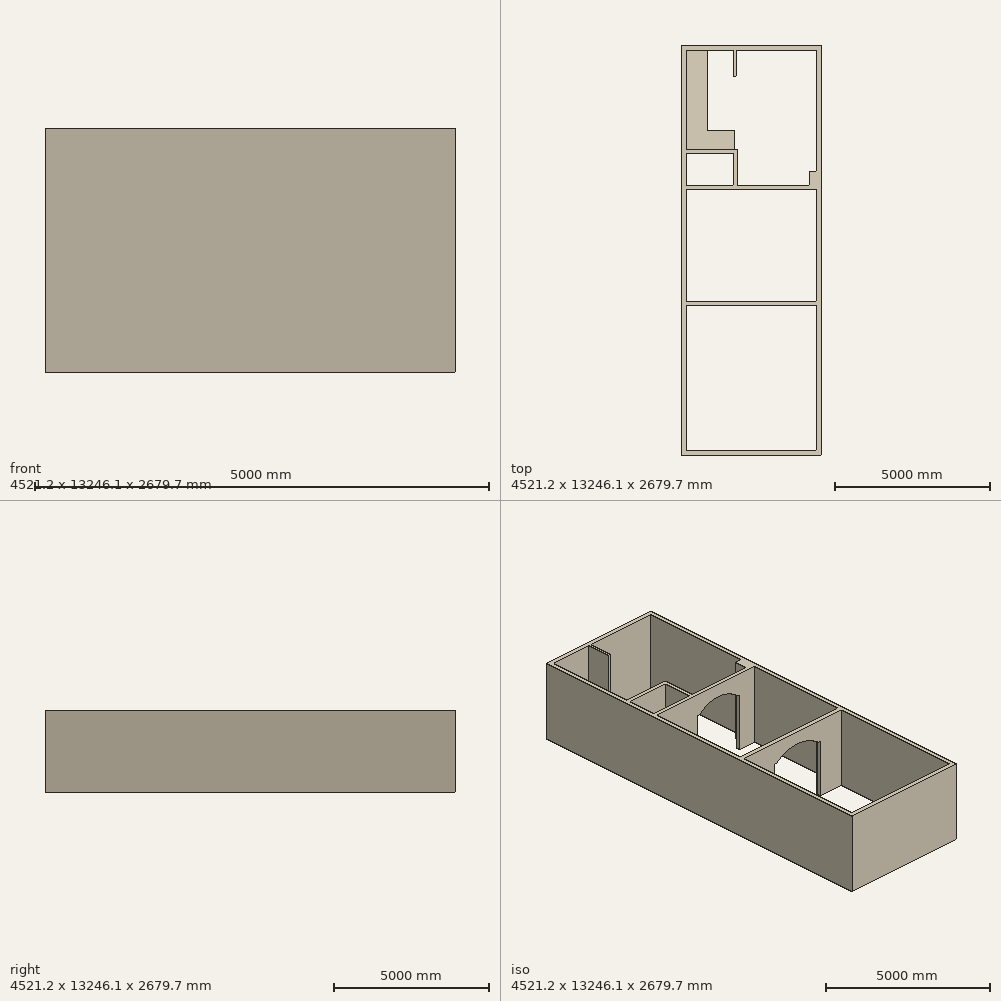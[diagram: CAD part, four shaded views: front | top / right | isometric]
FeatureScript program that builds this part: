
annotation { "Feature Type Name" : "Feature", "Feature Type Description" : "" }
export const myFeature = defineFeature(function(context is Context, id is Id, definition is map)
    precondition{}
    {
        {
            var Q0;
            Q0=qCreatedBy(makeId("Top.planeOp"),FACE);
            var sketch = newSketch(context, id + "F0", { "sketchPlane" : qUnion([Q0])});
            skLineSegment(sketch, "E0.bottom", {"start": v(0, 0) * mm, "end": v(4216.4, 0) * mm});
            skLineSegment(sketch, "E0.top", {"start": v(0, 12941.3) * mm, "end": v(1536.7, 12941.3) * mm});
            skLineSegment(sketch, "E0.left", {"start": v(0, 0) * mm, "end": v(0, 4686.3) * mm});
            skLineSegment(sketch, "E0.right", {"start": v(4216.4, 0) * mm, "end": v(4216.4, 4686.3) * mm});
            skLineSegment(sketch, "E1.bottom", {"start": v(4216.4, 4686.3) * mm, "end": v(3314.7, 4686.3) * mm});
            skLineSegment(sketch, "E1.top", {"start": v(4216.4, 4838.7) * mm, "end": v(3314.7, 4838.7) * mm});
            skLineSegment(sketch, "E1.right", {"start": v(3314.7, 4686.3) * mm, "end": v(3314.7, 4838.7) * mm});
            skLineSegment(sketch, "E2.0", {"start": v(-152.4, 13093.7) * mm, "end": v(4368.8, 13093.7) * mm});
            skLineSegment(sketch, "E2.1", {"start": v(-152.4, -152.4) * mm, "end": v(-152.4, 13093.7) * mm});
            skLineSegment(sketch, "E2.2", {"start": v(-152.4, -152.4) * mm, "end": v(4368.8, -152.4) * mm});
            skLineSegment(sketch, "E2.3", {"start": v(4368.8, -152.4) * mm, "end": v(4368.8, 13093.7) * mm});
            skLineSegment(sketch, "E3.trimOffspring", {"start": v(4216.4, 4838.7) * mm, "end": v(4216.4, 8445.5) * mm});
            skLineSegment(sketch, "E4", {"start": v(4216.4, 8445.5) * mm, "end": v(3581.4, 8445.5) * mm});
            skLineSegment(sketch, "E5", {"start": v(3581.4, 8445.5) * mm, "end": v(3581.4, 8572.5) * mm});
            skLineSegment(sketch, "E6", {"start": v(3581.4, 8572.5) * mm, "end": v(3987.8, 8572.5) * mm});
            skLineSegment(sketch, "E7.trimOffspring", {"start": v(4216.4, 9029.7) * mm, "end": v(4216.4, 12941.3) * mm});
            skLineSegment(sketch, "E8", {"start": v(3987.8, 8572.5) * mm, "end": v(3987.8, 9029.7) * mm});
            skLineSegment(sketch, "E9", {"start": v(3987.8, 9029.7) * mm, "end": v(4216.4, 9029.7) * mm});
            skLineSegment(sketch, "E10", {"start": v(1752.6, 8445.5) * mm, "end": v(0, 8445.5) * mm});
            skLineSegment(sketch, "E11", {"start": v(1752.6, 8445.5) * mm, "end": v(1752.6, 8572.5) * mm});
            skLineSegment(sketch, "E12", {"start": v(1752.6, 8572.5) * mm, "end": v(1663.7, 8572.5) * mm});
            skLineSegment(sketch, "E13", {"start": v(1663.7, 8572.5) * mm, "end": v(1663.7, 9740.9) * mm});
            skLineSegment(sketch, "E14", {"start": v(1663.7, 9740.9) * mm, "end": v(0, 9740.9) * mm});
            skLineSegment(sketch, "E15.0", {"start": v(1536.7, 9613.9) * mm, "end": v(0, 9613.9) * mm});
            skLineSegment(sketch, "E15.1", {"start": v(1536.7, 8572.5) * mm, "end": v(1536.7, 9613.9) * mm});
            skLineSegment(sketch, "E16", {"start": v(1536.7, 8572.5) * mm, "end": v(0, 8572.5) * mm});
            skLineSegment(sketch, "E17.trimOffspring", {"start": v(0, 8572.5) * mm, "end": v(0, 9613.9) * mm});
            skLineSegment(sketch, "E18.trimOffspring", {"start": v(0, 9740.9) * mm, "end": v(0, 12941.3) * mm});
            skLineSegment(sketch, "E19.top", {"start": v(1536.7, 12077.7) * mm, "end": v(1625.6, 12077.7) * mm});
            skLineSegment(sketch, "E19.left", {"start": v(1536.7, 12941.3) * mm, "end": v(1536.7, 12077.7) * mm});
            skLineSegment(sketch, "E19.right", {"start": v(1625.6, 12941.3) * mm, "end": v(1625.6, 12077.7) * mm});
            skLineSegment(sketch, "E20.trimOffspring", {"start": v(1625.6, 12941.3) * mm, "end": v(4216.4, 12941.3) * mm});
            skLineSegment(sketch, "E21.bottom", {"start": v(1333.5, 4838.7) * mm, "end": v(0, 4838.7) * mm});
            skLineSegment(sketch, "E21.top", {"start": v(1333.5, 4686.3) * mm, "end": v(0, 4686.3) * mm});
            skLineSegment(sketch, "E21.left", {"start": v(1333.5, 4838.7) * mm, "end": v(1333.5, 4686.3) * mm});
            skLineSegment(sketch, "E22.trimOffspring", {"start": v(0, 4838.7) * mm, "end": v(0, 8445.5) * mm});
            skSolve(sketch);
        }
        {
            var Q0;
            Q0=makeQuery(id+"F0.imprint","IMPRINT",FACE,{"disambiguationData":[TD([[makeQuery(id+"F0.imprint","IMPRINT",EDGE,{"derivedFrom":sQuery(id+"F0.wireOp",EDGE,"E0.bottom")}),-1.0]])]});
            extrude(context, id + "F1", {"entities" : qUnion([Q0]), "depth" : 2679.7 * mm});
        }
        {
            var Q0;
            Q0=makeQuery(id+"F1.opExtrude","SWEPT_FACE",FACE,{"disambiguationData":[OSD([sQuery(id+"F0.wireOp",EDGE,"E21.top")])]});
            var sketch = newSketch(context, id + "F2", { "sketchPlane" : qUnion([Q0])});
            skLineSegment(sketch, "E23.bottom", {"start": v(1333.5, 2679.7) * mm, "end": v(3314.7, 2679.7) * mm});
            skLineSegment(sketch, "E23.top", {"start": v(1333.5, 1930.4) * mm, "end": v(1422.4, 1930.4) * mm});
            skLineSegment(sketch, "E23.left", {"start": v(1333.5, 2679.7) * mm, "end": v(1333.5, 1930.4) * mm});
            skLineSegment(sketch, "E23.right", {"start": v(3314.7, 2679.7) * mm, "end": v(3314.7, 1930.4) * mm});
            skLineSegment(sketch, "E24", {"start": v(2324.1, 1930.4) * mm, "end": v(2324.1, 2679.7) * mm, "construction": true});
            skLineSegment(sketch, "E25", {"start": v(1422.4, 1930.4) * mm, "end": v(1422.4, 2679.7) * mm, "construction": true});
            skLineSegment(sketch, "E26", {"start": v(3225.8, 1930.4) * mm, "end": v(3225.8, 2679.7) * mm, "construction": true});
            skLineSegment(sketch, "E27", {"start": v(1422.4, 2247.9) * mm, "end": v(3225.8, 2247.9) * mm, "construction": true});
            skArc(sketch, "E28", {"start": v(3225.8, 1930.4) * mm, "mid": v(2324.1, 2247.9) * mm, "end": v(1422.4, 1930.4) * mm});
            skLineSegment(sketch, "E29.trimOffspring", {"start": v(3225.8, 1930.4) * mm, "end": v(3314.7, 1930.4) * mm});
            skSolve(sketch);
        }
        {
            var Q0;
            Q0=makeQuery(id+"F2.imprint","IMPRINT",FACE,{"disambiguationData":[TD([[makeQuery(id+"F2.imprint","IMPRINT",EDGE,{"derivedFrom":sQuery(id+"F2.wireOp",EDGE,"E23.bottom")}),-1.0]])]});
            extrude(context, id + "F3", {"entities" : qUnion([Q0]), "operationType" : NewBodyOperationType.ADD, "oppositeDirection" : true, "depth" : 152.4 * mm});
        }
        {
            var Q0;
            Q0=makeQuery(id+"F1.opExtrude","SWEPT_FACE",FACE,{"disambiguationData":[OSD([sQuery(id+"F0.wireOp",EDGE,"E10")])]});
            var sketch = newSketch(context, id + "F4", { "sketchPlane" : qUnion([Q0])});
            skLineSegment(sketch, "E30.bottom", {"start": v(1752.6, 2679.7) * mm, "end": v(3581.4, 2679.7) * mm});
            skLineSegment(sketch, "E30.top", {"start": v(1752.6, 1930.4) * mm, "end": v(1841.5, 1930.4) * mm});
            skLineSegment(sketch, "E30.left", {"start": v(1752.6, 2679.7) * mm, "end": v(1752.6, 1930.4) * mm});
            skLineSegment(sketch, "E30.right", {"start": v(3581.4, 2679.7) * mm, "end": v(3581.4, 1930.4) * mm});
            skLineSegment(sketch, "E31", {"start": v(2667, 1930.4) * mm, "end": v(2667, 2679.7) * mm, "construction": true});
            skLineSegment(sketch, "E32", {"start": v(1841.5, 1930.4) * mm, "end": v(1841.5, 2679.7) * mm, "construction": true});
            skLineSegment(sketch, "E33", {"start": v(3492.5, 1930.4) * mm, "end": v(3492.5, 2679.7) * mm, "construction": true});
            skLineSegment(sketch, "E34", {"start": v(1841.5, 2247.9) * mm, "end": v(3492.5, 2247.9) * mm, "construction": true});
            skArc(sketch, "E35", {"start": v(3492.5, 1930.4) * mm, "mid": v(2667, 2247.9) * mm, "end": v(1841.5, 1930.4) * mm});
            skLineSegment(sketch, "E36.trimOffspring", {"start": v(3492.5, 1930.4) * mm, "end": v(3581.4, 1930.4) * mm});
            skSolve(sketch);
        }
        {
            var Q0;
            Q0 = qSketchRegion(id + "F4", true);
            extrude(context, id + "F5", {"entities" : qUnion([Q0]), "operationType" : NewBodyOperationType.ADD, "oppositeDirection" : true, "depth" : 127 * mm});
        }
        {
            var Q0;
            Q0=makeQuery(id+"F1.opExtrude","CAP_FACE",FACE,{"disambiguationData":[OSD([sQuery(id+"F0.wireOp",EDGE,"E0.bottom"),sQuery(id+"F0.wireOp",EDGE,"E0.top"),sQuery(id+"F0.wireOp",EDGE,"E0.left"),sQuery(id+"F0.wireOp",EDGE,"E0.right"),sQuery(id+"F0.wireOp",EDGE,"E1.bottom"),sQuery(id+"F0.wireOp",EDGE,"E1.top"),sQuery(id+"F0.wireOp",EDGE,"E1.right"),sQuery(id+"F0.wireOp",EDGE,"E2.0"),sQuery(id+"F0.wireOp",EDGE,"E2.1"),sQuery(id+"F0.wireOp",EDGE,"E2.2"),sQuery(id+"F0.wireOp",EDGE,"E2.3"),sQuery(id+"F0.wireOp",EDGE,"E3.trimOffspring"),sQuery(id+"F0.wireOp",EDGE,"E4"),sQuery(id+"F0.wireOp",EDGE,"E5"),sQuery(id+"F0.wireOp",EDGE,"E6"),sQuery(id+"F0.wireOp",EDGE,"E7.trimOffspring"),sQuery(id+"F0.wireOp",EDGE,"E8"),sQuery(id+"F0.wireOp",EDGE,"E9"),sQuery(id+"F0.wireOp",EDGE,"E10"),sQuery(id+"F0.wireOp",EDGE,"E11"),sQuery(id+"F0.wireOp",EDGE,"E12"),sQuery(id+"F0.wireOp",EDGE,"E13"),sQuery(id+"F0.wireOp",EDGE,"E14"),sQuery(id+"F0.wireOp",EDGE,"E15.0"),sQuery(id+"F0.wireOp",EDGE,"E15.1"),sQuery(id+"F0.wireOp",EDGE,"E16"),sQuery(id+"F0.wireOp",EDGE,"E17.trimOffspring"),sQuery(id+"F0.wireOp",EDGE,"E18.trimOffspring"),sQuery(id+"F0.wireOp",EDGE,"E19.top"),sQuery(id+"F0.wireOp",EDGE,"E19.left"),sQuery(id+"F0.wireOp",EDGE,"E19.right"),sQuery(id+"F0.wireOp",EDGE,"E20.trimOffspring"),sQuery(id+"F0.wireOp",EDGE,"E21.bottom"),sQuery(id+"F0.wireOp",EDGE,"E21.top"),sQuery(id+"F0.wireOp",EDGE,"E21.left"),sQuery(id+"F0.wireOp",EDGE,"E22.trimOffspring")])],"isStart":true});
            var sketch = newSketch(context, id + "F6", { "sketchPlane" : qUnion([Q0])});
            skLineSegment(sketch, "E37.bottom", {"start": v(0, -12941.3) * mm, "end": v(673.1, -12941.3) * mm});
            skLineSegment(sketch, "E37.top", {"start": v(0, -9740.9) * mm, "end": v(1562.1, -9740.9) * mm});
            skLineSegment(sketch, "E37.left", {"start": v(0, -12941.3) * mm, "end": v(0, -9740.9) * mm});
            skLineSegment(sketch, "E38.top", {"start": v(1562.1, -10337.8) * mm, "end": v(673.1, -10337.8) * mm});
            skLineSegment(sketch, "E38.left", {"start": v(1562.1, -9740.9) * mm, "end": v(1562.1, -10337.8) * mm});
            skLineSegment(sketch, "E39", {"start": v(673.1, -10337.8) * mm, "end": v(673.1, -12941.3) * mm});
            skSolve(sketch);
        }
        {
            var Q0;
            Q0 = qSketchRegion(id + "F6", true);
            extrude(context, id + "F7", {"entities" : qUnion([Q0]), "operationType" : NewBodyOperationType.ADD, "oppositeDirection" : true, "depth" : 914.4 * mm});
        }
        {
            var Q0;
            Q0=makeQuery(id+"F1.opExtrude","SWEPT_FACE",FACE,{"disambiguationData":[OSD([sQuery(id+"F0.wireOp",EDGE,"E13")])]});
            var sketch = newSketch(context, id + "F8", { "sketchPlane" : qUnion([Q0])});
            skLineSegment(sketch, "E40.bottom", {"start": v(8661.4, 0) * mm, "end": v(9372.6, 0) * mm});
            skLineSegment(sketch, "E40.top", {"start": v(8661.4, 1955.8) * mm, "end": v(9372.6, 1955.8) * mm});
            skLineSegment(sketch, "E40.left", {"start": v(8661.4, 0) * mm, "end": v(8661.4, 1955.8) * mm});
            skLineSegment(sketch, "E40.right", {"start": v(9372.6, 0) * mm, "end": v(9372.6, 1955.8) * mm});
            skSolve(sketch);
        }
        {
            var Q0;
            Q0 = qSketchRegion(id + "F8", true);
            extrude(context, id + "F9", {"entities" : qUnion([Q0]), "operationType" : NewBodyOperationType.REMOVE, "endBound" : BoundingType.UP_TO_NEXT, "oppositeDirection" : true, "depth" : 25.4 * mm});
        }
    });
